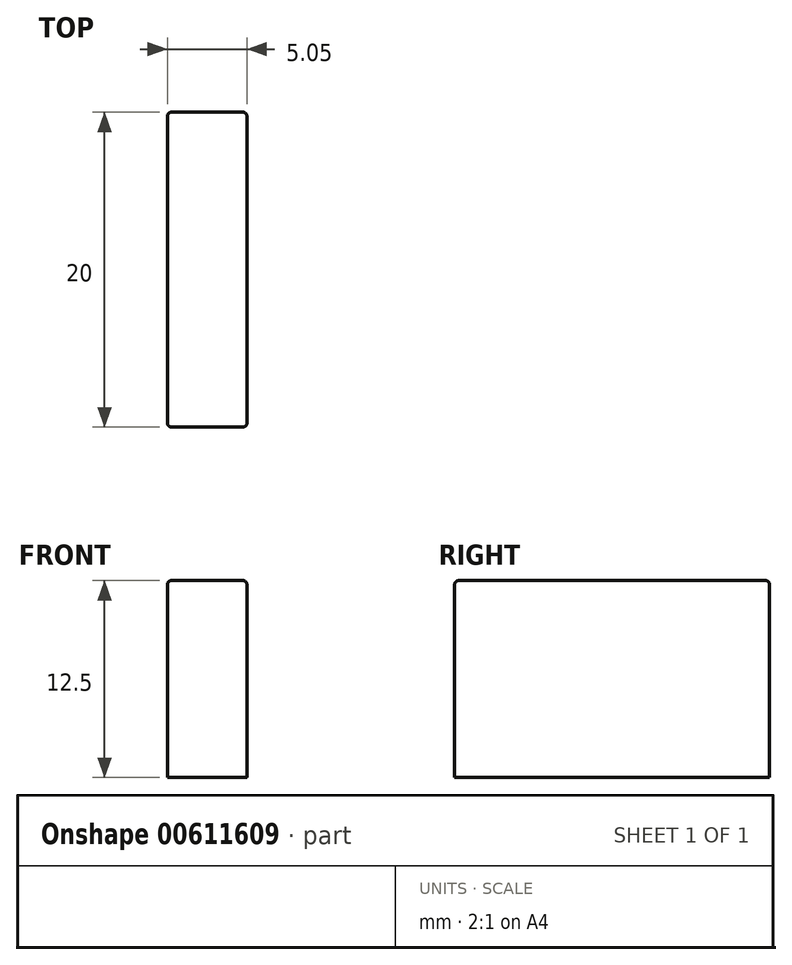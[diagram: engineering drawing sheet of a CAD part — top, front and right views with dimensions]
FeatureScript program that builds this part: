
annotation { "Feature Type Name" : "Feature", "Feature Type Description" : "" }
export const myFeature = defineFeature(function(context is Context, id is Id, definition is map)
    precondition{}
    {
        {
            var Q0;
            Q0=qCreatedBy(makeId("Top.planeOp"),FACE);
            var sketch = newSketch(context, id + "F0", { "sketchPlane" : qUnion([Q0])});
            skLineSegment(sketch, "E0.bottom", {"start": v(2.54, 2.54) * mm, "end": v(7.6, 2.54) * mm});
            skLineSegment(sketch, "E0.top", {"start": v(2.54, 22.54) * mm, "end": v(7.59, 22.54) * mm});
            skLineSegment(sketch, "E0.left", {"start": v(2.54, 2.54) * mm, "end": v(2.54, 22.54) * mm});
            skLineSegment(sketch, "E0.right", {"start": v(7.6, 2.54) * mm, "end": v(7.59, 22.54) * mm});
            skSolve(sketch);
        }
        {
            var Q0;
            Q0 = qSketchRegion(id + "F0", true);
            extrude(context, id + "F1", {"entities" : qUnion([Q0]), "depth" : 12.5 * mm, "offsetDistance" : 25 * mm});
        }
        {
            var Q0;
            Q0=makeQuery(id+"F1.opExtrude","CAP_EDGE",EDGE,{"disambiguationData":[OSD([sQuery(id+"F0.wireOp",EDGE,"E0.right")])],"isStart":false});
            var Q1;
            Q1=makeQuery(id+"F1.opExtrude","SWEPT_EDGE",EDGE,{"disambiguationData":[OSD([sQuery(id+"F0.wireOp",EDGE,"E0.bottom"),sQuery(id+"F0.wireOp",EDGE,"E0.right")])]});
            var Q2;
            Q2=makeQuery(id+"F1.opExtrude","CAP_EDGE",EDGE,{"disambiguationData":[OSD([sQuery(id+"F0.wireOp",EDGE,"E0.bottom")])],"isStart":false});
            var Q3;
            Q3=makeQuery(id+"F1.opExtrude","SWEPT_EDGE",EDGE,{"disambiguationData":[OSD([sQuery(id+"F0.wireOp",EDGE,"E0.bottom"),sQuery(id+"F0.wireOp",EDGE,"E0.left")])]});
            var Q4;
            Q4=makeQuery(id+"F1.opExtrude","CAP_EDGE",EDGE,{"disambiguationData":[OSD([sQuery(id+"F0.wireOp",EDGE,"E0.left")])],"isStart":false});
            var Q5;
            Q5=makeQuery(id+"F1.opExtrude","SWEPT_EDGE",EDGE,{"disambiguationData":[OSD([sQuery(id+"F0.wireOp",EDGE,"E0.top"),sQuery(id+"F0.wireOp",EDGE,"E0.right")])]});
            var Q6;
            Q6=makeQuery(id+"F1.opExtrude","CAP_EDGE",EDGE,{"disambiguationData":[OSD([sQuery(id+"F0.wireOp",EDGE,"E0.top")])],"isStart":false});
            var Q7;
            Q7=makeQuery(id+"F1.opExtrude","SWEPT_EDGE",EDGE,{"disambiguationData":[OSD([sQuery(id+"F0.wireOp",EDGE,"E0.top"),sQuery(id+"F0.wireOp",EDGE,"E0.left")])]});
            fillet(context, id + "F2", {"entities" : qUnion([Q0, Q1, Q2, Q3, Q4, Q5, Q6, Q7]), "radius" : .25 * mm, "tangentPropagation" : true, "allowEdgeOverflow" : false});
        }
    });
